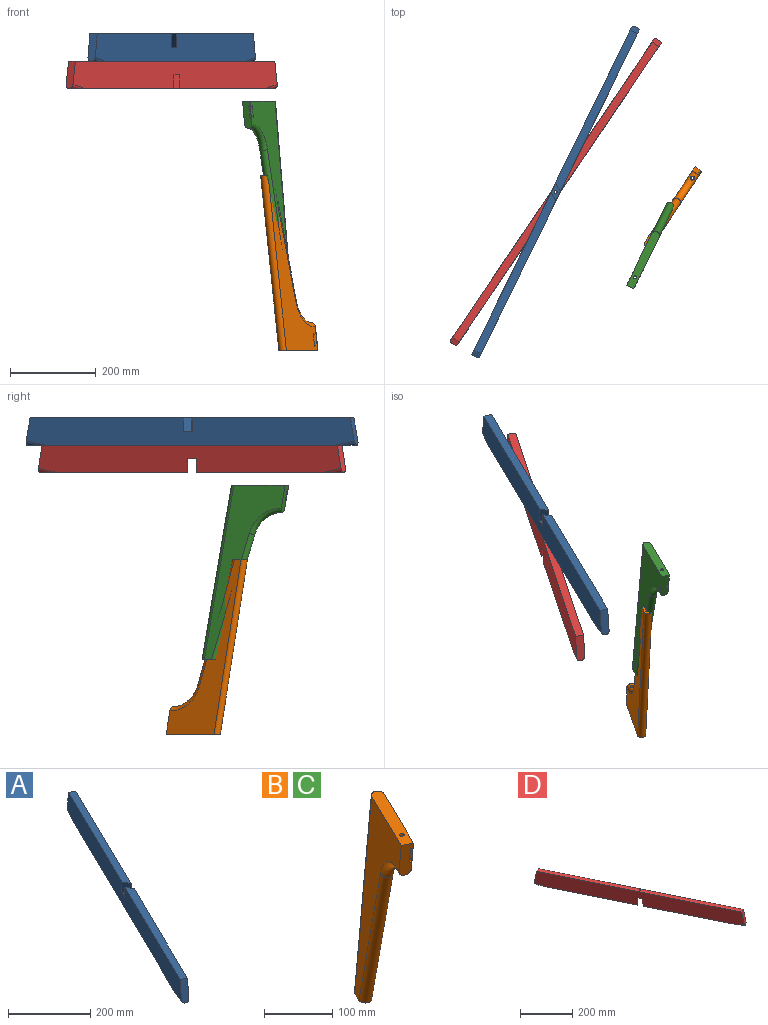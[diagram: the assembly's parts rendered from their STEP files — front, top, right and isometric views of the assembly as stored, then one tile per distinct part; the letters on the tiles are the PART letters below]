
ASSEMBLY  parts=4 mates=1
PART A: 16 faces, bbox 390.6x774.6x72.9 mm
  f0: plane 768.85x377.94mm, normal (0,0,-1), area 15793.9mm2, adj f1,f2,f10,f13,f14,f15
  f1: plane 765.63x373.42mm, normal (-0.9,0.44,0), area 52327.6mm2, adj f0,f3,f4,f5,f6,f7,f8,f9
  f2: plane 765.63x373.42mm, normal (0.9,-0.44,0), area 52327.6mm2, adj f0,f3,f4,f5,f6,f7,f8,f9
  f3: plane 63.44x21.6mm, normal (0.43,0.88,0.18), area 1190.6mm2, adj f1,f2,f6,f13
  f4: plane 377.68x191.19mm, normal (0,0,1), area 7696.2mm2, adj f1,f2,f5,f9
  f5: plane 63.5x21.61mm, normal (-0.43,-0.88,0.18), area 1191.8mm2, adj f1,f2,f4,f14,f15
  f6: plane 377.68x191.19mm, normal (0,0,1), area 7696.2mm2, adj f1,f2,f3,f8
  f7: plane 41.96x21.38mm, normal (0,0,1), area 416.9mm2, adj f1,f2,f8,f9,f12
  f8: plane 31.75x20.79mm, normal (-0.88,-0.47,0), area 747.6mm2, adj f1,f2,f6,f7
  f9: plane 31.75x20.79mm, normal (0.88,0.47,0), area 747.6mm2, adj f1,f2,f4,f7
  f10: cylinder r=4.76mm len=12.7mm, axis (0,0,-1), area 380mm2, adj f0,f11
  f11: plane 9.53x9.53mm, normal (0,0,-1), area 39.6mm2, adj f10,f12
  f12: cylinder r=3.17mm len=19.05mm, axis (0,0,-1), area 380mm2, adj f7,f11
  f13: cylinder r=9.53mm len=53.51mm, axis (0.43,0.88,0.18), area 556.2mm2, adj f0,f1,f2,f3
  f14: cylinder r=9.53mm len=47.76mm, axis (-0.43,-0.88,0.18), area 276.2mm2, adj f0,f2,f5
  f15: cylinder r=9.53mm len=50.63mm, axis (-0.43,-0.88,0.18), area 276.2mm2, adj f0,f1,f5
PART B: 16 faces, bbox 110.1x202.2x411.2 mm
  f0: plane 63.5x21.6mm, normal (-0.43,-0.88,-0.18), area 1093.8mm2, adj f1,f3,f4,f6,f11,f12,f13,f14
  f1: plane 133.68x76.57mm, normal (0,0,1), area 2649.2mm2, adj f0,f3,f4,f7,f8
  f2: plane 36.11x27.24mm, normal (0,0,-1), area 645.1mm2, adj f3,f4,f5,f7
  f3: plane 406.4x188.33mm, normal (-0.9,0.44,0), area 23434.2mm2, adj f0,f1,f2,f5,f6,f7
  f4: plane 406.4x188.33mm, normal (0.9,-0.44,0), area 23434.2mm2, adj f0,f1,f2,f5,f6,f7
  f5: cylinder r=9.53mm len=296.82mm, axis (0.14,0.28,-0.95), area 9206.9mm2, adj f2,f3,f4,f6
  f6: torus R=85.72mm, axis (-0.9,0.44,0), area 2921.9mm2, adj f0,f3,f4,f5,f10
  f7: cylinder r=9.53mm len=409.92mm, axis (-0.08,-0.17,0.98), area 12372.9mm2, adj f1,f2,f3,f4
  f8: cylinder r=3.38mm len=50.8mm, axis (0,0,1), area 1078.3mm2, adj f1,f9
  f9: plane 9.53x9.53mm, normal (0,0,-1), area 35.4mm2, adj f8,f10
  f10: cylinder r=4.76mm len=14.92mm, axis (0,0,1), area 399.4mm2, adj f6,f9
  f11: cylinder r=1.8mm len=11.74mm, axis (-0.43,-0.88,-0.18), area 64.7mm2, adj f0,f12,f14,f15
  f12: plane 27.72x14.23mm, normal (-0.9,0.44,-0.02), area 297.9mm2, adj f0,f11,f13,f15
  f13: cylinder r=1.59mm len=11.54mm, axis (-0.43,-0.88,-0.18), area 56.7mm2, adj f0,f12,f14,f15
  f14: plane 27.75x14.42mm, normal (0.9,-0.44,0), area 298.2mm2, adj f0,f11,f13,f15
  f15: plane 28.95x5.81mm, normal (-0.43,-0.88,-0.18), area 97.4mm2, adj f11,f12,f13,f14
PART C: same geometry as B
PART D: 15 faces, bbox 390.6x774.6x72.9 mm
  f0: plane 63.5x21.61mm, normal (0.43,-0.88,0.18), area 1191.8mm2, adj f3,f4,f6,f13,f14
  f1: plane 384.4x189.41mm, normal (0,0,-1), area 7711.7mm2, adj f3,f4,f8,f13,f14
  f2: plane 384.4x189.41mm, normal (0,0,-1), area 7711.7mm2, adj f3,f4,f9,f11,f12
  f3: plane 765.63x373.42mm, normal (0.9,0.44,0), area 52327.6mm2, adj f0,f1,f2,f5,f6,f7,f8,f9
  f4: plane 765.63x373.42mm, normal (-0.9,-0.44,0), area 52327.6mm2, adj f0,f1,f2,f5,f6,f7,f8,f9
  f5: plane 63.5x21.61mm, normal (-0.43,0.88,0.18), area 1191.8mm2, adj f3,f4,f6,f11,f12
  f6: plane 755.74x381.65mm, normal (0,0,1), area 15805.1mm2, adj f0,f3,f4,f5,f10
  f7: plane 41.96x21.38mm, normal (0,0,-1), area 412.7mm2, adj f3,f4,f8,f9,f10
  f8: plane 31.75x20.79mm, normal (-0.88,0.47,0), area 747.6mm2, adj f1,f3,f4,f7
  f9: plane 31.75x20.79mm, normal (0.88,-0.47,0), area 747.6mm2, adj f2,f3,f4,f7
  f10: cylinder r=3.38mm len=31.75mm, axis (0,0,-1), area 673.9mm2, adj f6,f7
  f11: cylinder r=9.53mm len=50.63mm, axis (-0.43,0.88,0.18), area 276.2mm2, adj f2,f4,f5
  f12: cylinder r=9.53mm len=47.76mm, axis (-0.43,0.88,0.18), area 276.2mm2, adj f2,f3,f5
  f13: cylinder r=9.53mm len=50.63mm, axis (0.43,-0.88,0.18), area 276.2mm2, adj f0,f1,f3
  f14: cylinder r=9.53mm len=47.76mm, axis (0.43,-0.88,0.18), area 276.2mm2, adj f0,f1,f4
PLACE A t=(-229.22,-140.09,401.11)mm fixed
PLACE B rot(axis=(0.87,-0.5,0),180deg) t=(333.63,261.27,-1038.16)mm
PLACE C t=(-237.42,-735.19,244.39)mm fixed
PLACE D rot(axis=(0,0,-1),60deg) t=(-229.22,-140.09,367.67)mm
MATE revolute D.f10 <-> A.f12  axis (0,0,1) through (-229.22,-140.09,-13.33)mm
